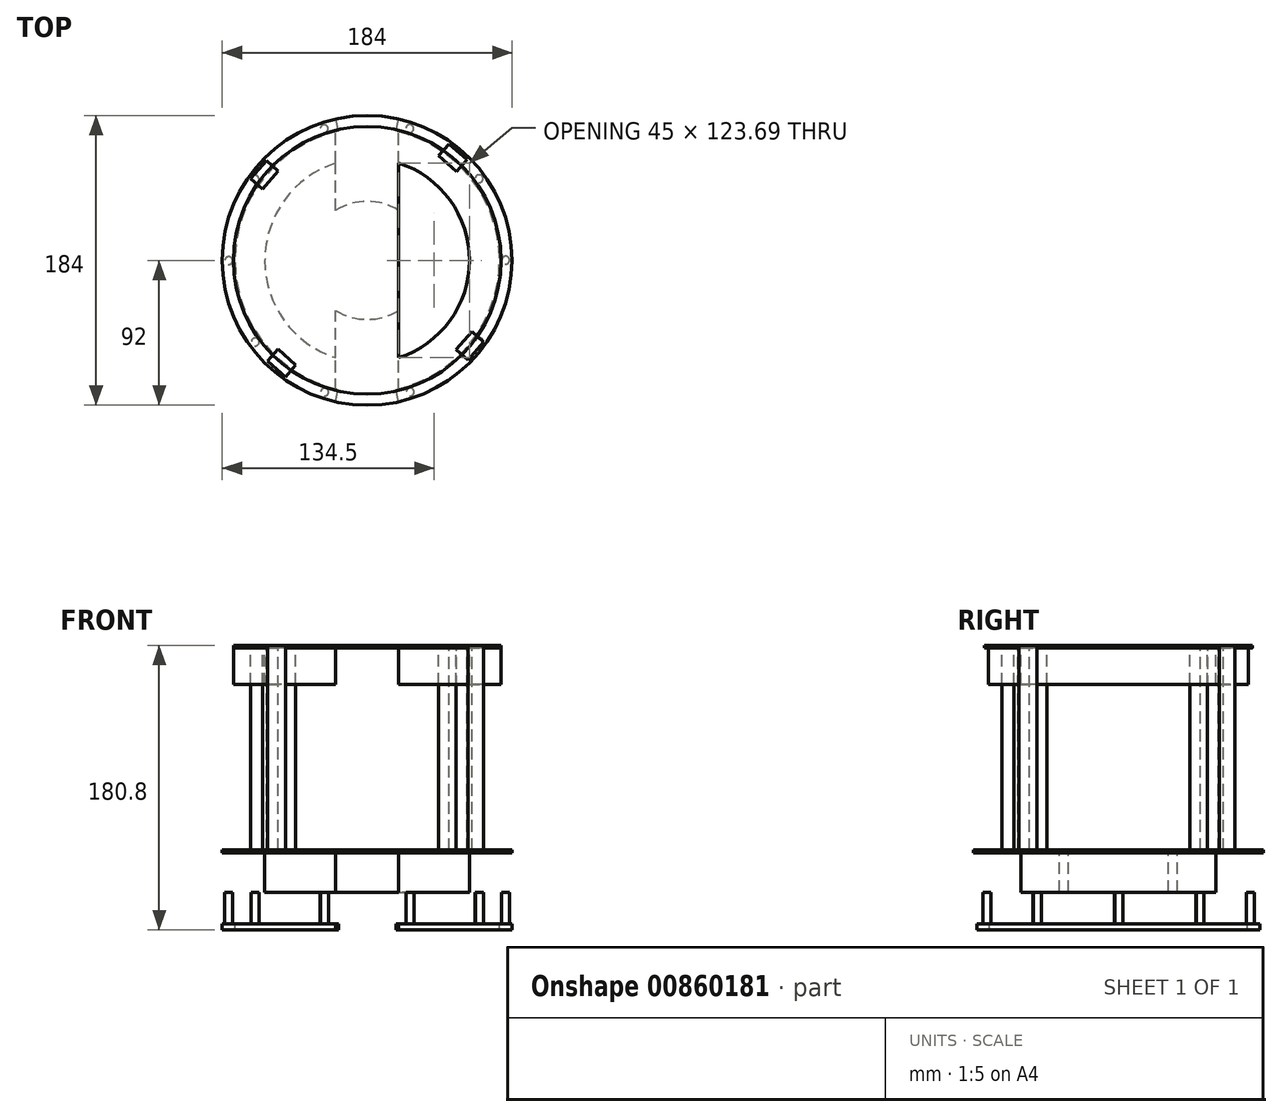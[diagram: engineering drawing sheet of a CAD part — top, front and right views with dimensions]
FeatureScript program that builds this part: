
annotation { "Feature Type Name" : "Feature", "Feature Type Description" : "" }
export const myFeature = defineFeature(function(context is Context, id is Id, definition is map)
    precondition{}
    {
        {
            var Q0;
            Q0=qCreatedBy(makeId("Top.planeOp"),FACE);
            var sketch = newSketch(context, id + "F0", { "sketchPlane" : qUnion([Q0])});
            skCircle(sketch, "E0", {"center": v(0, 0) * mm, "radius": 85 * mm});
            skLineSegment(sketch, "E1", {"start": v(0, 0) * mm, "end": v(15, 0) * mm, "construction": true});
            skLineSegment(sketch, "E2", {"start": v(0, 0) * mm, "end": v(-15, 0) * mm, "construction": true});
            skLineSegment(sketch, "E3", {"start": v(0, 0) * mm, "end": v(0, -65) * mm, "construction": true});
            skLineSegment(sketch, "E4", {"start": v(0, 0) * mm, "end": v(0, 65) * mm, "construction": true});
            skLineSegment(sketch, "E5", {"start": v(0, 65) * mm, "end": v(15, 65) * mm, "construction": true});
            skLineSegment(sketch, "E6", {"start": v(0, 65) * mm, "end": v(-15, 65) * mm, "construction": true});
            skCircle(sketch, "E7", {"center": v(0, 0) * mm, "radius": 65 * mm});
            skLineSegment(sketch, "E8.bottom", {"start": v(20, -93.84) * mm, "end": v(-20, -93.84) * mm});
            skLineSegment(sketch, "E8.top", {"start": v(20, 93.84) * mm, "end": v(-20, 93.84) * mm});
            skLineSegment(sketch, "E8.left", {"start": v(20, -93.84) * mm, "end": v(20, 93.84) * mm});
            skLineSegment(sketch, "E8.right", {"start": v(-20, -93.84) * mm, "end": v(-20, 93.84) * mm});
            skSolve(sketch);
        }
        {
            var Q0;
            Q0=qCreatedBy(makeId("Top.planeOp"),FACE);
            var sketch = newSketch(context, id + "F1", { "sketchPlane" : qUnion([Q0])});
            skCircle(sketch, "E9.0", {"center": v(0, 0) * mm, "radius": 85 * mm});
            skSolve(sketch);
        }
        {
            var Q0;
            Q0=makeQuery(id+"F1.imprint","IMPRINT",FACE,{"disambiguationData":[TD([[makeQuery(id+"F1.imprint","IMPRINT",EDGE,{"derivedFrom":sQuery(id+"F1.wireOp",EDGE,"E9.0")}),1.0]])]});
            extrude(context, id + "F2", {"entities" : qUnion([Q0]), "oppositeDirection" : true, "depth" : 1.8 * mm, "offsetDistance" : 25 * mm});
        }
        {
            var Q0;
            {var subQ0=sQuery(id+"F0.wireOp",EDGE,"E8.left");var subQ1=sQuery(id+"F0.wireOp",EDGE,"E0");var subQ2=makeQuery(id+"F0.imprint","INTERSECT",VERTEX,{"disambiguationData":[OD(0.0)],"derivedFrom":[subQ1,subQ0]});Q0=makeQuery(id+"F0.imprint","IMPRINT",FACE,{"disambiguationData":[TD([[makeQuery(id+"F0.imprint","IMPRINT",EDGE,{"disambiguationData":[TD([[subQ2,1.0]])],"derivedFrom":subQ1}),1.0]])]});}
            var Q1;
            {var subQ0=sQuery(id+"F0.wireOp",EDGE,"E8.right");var subQ1=sQuery(id+"F0.wireOp",EDGE,"E0");var subQ2=makeQuery(id+"F0.imprint","INTERSECT",VERTEX,{"disambiguationData":[OD(0.0)],"derivedFrom":[subQ1,subQ0]});Q1=makeQuery(id+"F0.imprint","IMPRINT",FACE,{"disambiguationData":[TD([[makeQuery(id+"F0.imprint","IMPRINT",EDGE,{"disambiguationData":[TD([[subQ2,-1.0]])],"derivedFrom":subQ1}),1.0]])]});}
            extrude(context, id + "F3", {"entities" : qUnion([Q0, Q1]), "operationType" : NewBodyOperationType.ADD, "oppositeDirection" : true, "depth" : 25 * mm, "offsetDistance" : 25 * mm});
        }
        {
            var Q0;
            {var subQ0=sQuery(id+"F0.wireOp",EDGE,"E8.right");var subQ1=sQuery(id+"F0.wireOp",EDGE,"E0");var subQ2=makeQuery(id+"F0.imprint","INTERSECT",VERTEX,{"disambiguationData":[OD(0.0)],"derivedFrom":[subQ1,subQ0]});Q0=makeQuery(id+"F0.imprint","IMPRINT",FACE,{"disambiguationData":[TD([[makeQuery(id+"F0.imprint","IMPRINT",EDGE,{"disambiguationData":[TD([[subQ2,-1.0]])],"derivedFrom":subQ1}),1.0]])]});}
            var Q1;
            {var subQ0=sQuery(id+"F0.wireOp",EDGE,"E8.right");var subQ1=sQuery(id+"F0.wireOp",EDGE,"E0");var subQ2=makeQuery(id+"F0.imprint","INTERSECT",VERTEX,{"disambiguationData":[OD(0.0)],"derivedFrom":[subQ1,subQ0]});Q1=makeQuery(id+"F0.imprint","IMPRINT",FACE,{"disambiguationData":[TD([[makeQuery(id+"F0.imprint","IMPRINT",EDGE,{"disambiguationData":[TD([[subQ2,1.0]])],"derivedFrom":subQ1}),1.0]])]});}
            var Q2;
            {var subQ0=sQuery(id+"F0.wireOp",EDGE,"E8.left");var subQ1=sQuery(id+"F0.wireOp",EDGE,"E0");var subQ2=makeQuery(id+"F0.imprint","INTERSECT",VERTEX,{"disambiguationData":[OD(0.0)],"derivedFrom":[subQ1,subQ0]});Q2=makeQuery(id+"F0.imprint","IMPRINT",FACE,{"disambiguationData":[TD([[makeQuery(id+"F0.imprint","IMPRINT",EDGE,{"disambiguationData":[TD([[subQ2,1.0]])],"derivedFrom":subQ1}),1.0]])]});}
            var Q3;
            {var subQ0=sQuery(id+"F0.wireOp",EDGE,"E8.right");var subQ1=sQuery(id+"F0.wireOp",EDGE,"E0");var subQ2=makeQuery(id+"F0.imprint","INTERSECT",VERTEX,{"disambiguationData":[OD(1.0)],"derivedFrom":[subQ1,subQ0]});Q3=makeQuery(id+"F0.imprint","IMPRINT",FACE,{"disambiguationData":[TD([[makeQuery(id+"F0.imprint","IMPRINT",EDGE,{"disambiguationData":[TD([[subQ2,-1.0]])],"derivedFrom":subQ1}),1.0]])]});}
            var Q4;
            {var subQ0=sQuery(id+"F0.wireOp",EDGE,"E8.left");var subQ1=sQuery(id+"F0.wireOp",EDGE,"E7");var subQ2=makeQuery(id+"F0.imprint","INTERSECT",VERTEX,{"disambiguationData":[OD(0.0)],"derivedFrom":[subQ1,subQ0]});Q4=makeQuery(id+"F0.imprint","IMPRINT",FACE,{"disambiguationData":[TD([[makeQuery(id+"F0.imprint","IMPRINT",EDGE,{"disambiguationData":[TD([[subQ2,1.0]])],"derivedFrom":subQ1}),1.0]])]});}
            var Q5;
            {var subQ0=sQuery(id+"F0.wireOp",EDGE,"E8.right");var subQ1=sQuery(id+"F0.wireOp",EDGE,"E7");var subQ2=makeQuery(id+"F0.imprint","INTERSECT",VERTEX,{"disambiguationData":[OD(0.0)],"derivedFrom":[subQ1,subQ0]});Q5=makeQuery(id+"F0.imprint","IMPRINT",FACE,{"disambiguationData":[TD([[makeQuery(id+"F0.imprint","IMPRINT",EDGE,{"disambiguationData":[TD([[subQ2,-1.0]])],"derivedFrom":subQ1}),1.0]])]});}
            var Q6;
            {var subQ0=sQuery(id+"F0.wireOp",EDGE,"E8.right");var subQ1=sQuery(id+"F0.wireOp",EDGE,"E7");var subQ2=makeQuery(id+"F0.imprint","INTERSECT",VERTEX,{"disambiguationData":[OD(0.0)],"derivedFrom":[subQ1,subQ0]});Q6=makeQuery(id+"F0.imprint","IMPRINT",FACE,{"disambiguationData":[TD([[makeQuery(id+"F0.imprint","IMPRINT",EDGE,{"disambiguationData":[TD([[subQ2,1.0]])],"derivedFrom":subQ1}),1.0]])]});}
            extrude(context, id + "F4", {"entities" : qUnion([Q0, Q1, Q2, Q3, Q4, Q5, Q6]), "oppositeDirection" : true, "depth" : 1.8 * mm, "offsetDistance" : 25 * mm});
        }
        {
            var Q0;
            {var subQ0=sQuery(id+"F0.wireOp",EDGE,"E0");Q0=makeQuery(id+"F92N3ToIArTKFft_1.boolean.opBoolean","SPLIT",FACE,{"disambiguationData":[TD([makeQuery(id+"FFIeb2ztRoP1rm2_1.boolean.opBoolean","COPY",FACE,{"derivedFrom":makeQuery(id+"FFIeb2ztRoP1rm2_1.opExtrude","SWEPT_FACE",FACE,{"disambiguationData":[OSD([sQuery(id+"FUWerJDIJFKlQu6_1.wireOp",EDGE,"KzpTdK0h-yw9V-XJjy-UJbk-oXAReHN1zFgU.left")])]})})])],"derivedFrom":makeQuery(id+"F4.opExtrude","CAP_FACE",FACE,{"disambiguationData":[OSD([subQ0])],"isStart":true})});}
            var sketch = newSketch(context, id + "F5", { "sketchPlane" : qUnion([Q0])});
            skLineSegment(sketch, "E10", {"start": v(-25, 60) * mm, "end": v(-60.2, 60) * mm, "construction": true});
            skLineSegment(sketch, "E11", {"start": v(-60.2, 60) * mm, "end": v(-45.17, 46.74) * mm, "construction": true});
            skLineSegment(sketch, "E12", {"start": v(-60.2, 60) * mm, "end": v(-56.46, 56.7) * mm});
            skLineSegment(sketch, "E13", {"start": v(-56.46, 56.7) * mm, "end": v(-66.46, 45.34) * mm});
            skLineSegment(sketch, "E14", {"start": v(-66.46, 45.34) * mm, "end": v(-73.96, 51.96) * mm});
            skLineSegment(sketch, "E15", {"start": v(-73.96, 51.96) * mm, "end": v(-63.96, 63.3) * mm});
            skLineSegment(sketch, "E16", {"start": v(-63.96, 63.3) * mm, "end": v(-56.46, 56.7) * mm});
            skSolve(sketch);
        }
        {
            var Q0;
            {var subQ0=sQuery(id+"F5.wireOp",EDGE,"E15");Q0=makeQuery(id+"F5.imprint","IMPRINT",FACE,{"disambiguationData":[TD([[makeQuery(id+"F5.imprint","IMPRINT",EDGE,{"derivedFrom":subQ0}),-1.0]])]});}
            var Q1;
            {var subQ0=sQuery(id+"F5.wireOp",EDGE,"E13");Q1=makeQuery(id+"F5.imprint","IMPRINT",FACE,{"disambiguationData":[TD([[makeQuery(id+"F5.imprint","IMPRINT",EDGE,{"derivedFrom":subQ0}),-1.0]])]});}
            extrude(context, id + "F6", {"entities" : qUnion([Q0, Q1]), "oppositeDirection" : true, "depth" : 130 * mm, "offsetDistance" : 25 * mm});
        }
        {
            var Q0;
            Q0=qCreatedBy(makeId("Right.planeOp"),FACE);
            var sketch = newSketch(context, id + "F7", { "sketchPlane" : qUnion([Q0])});
            skLineSegment(sketch, "E17", {"start": v(0, 0) * mm, "end": v(0, 63.94) * mm, "construction": true});
            skSolve(sketch);
        }
        {
            var Q0;
            Q0=makeQuery(id+"F6.opExtrude","SWEPT_BODY",BODY,{"disambiguationData":[OSD([sQuery(id+"F5.wireOp",EDGE,"E13"),sQuery(id+"F5.wireOp",EDGE,"E14"),sQuery(id+"F5.wireOp",EDGE,"E15"),sQuery(id+"F5.wireOp",EDGE,"E16")])]});
            var Q1;
            Q1=sQuery(id+"F7.wireOp",EDGE,"E17");
            circularPattern(context, id + "F8", {"entities" : qUnion([Q0]), "axis" : qUnion([Q1]), "angle" : 360 * degree, "instanceCount" : 4, "equalSpace" : true});
        }
        {
            var Q0;
            Q0=makeQuery(id+"F6.opExtrude","CAP_FACE",FACE,{"disambiguationData":[OSD([sQuery(id+"F5.wireOp",EDGE,"E13"),sQuery(id+"F5.wireOp",EDGE,"E14"),sQuery(id+"F5.wireOp",EDGE,"E15"),sQuery(id+"F5.wireOp",EDGE,"E16")])],"isStart":false});
            var sketch = newSketch(context, id + "F9", { "sketchPlane" : qUnion([Q0])});
            skCircle(sketch, "E18", {"center": v(0, 0) * mm, "radius": 92 * mm});
            skSolve(sketch);
        }
        {
            var Q0;
            Q0=makeQuery(id+"F9.imprint","IMPRINT",FACE,{"disambiguationData":[TD([[makeQuery(id+"F9.imprint","IMPRINT",EDGE,{"derivedFrom":sQuery(id+"F9.wireOp",EDGE,"E18")}),1.0]])]});
            var Q1;
            Q1=makeQuery(id+"F9.imprint","IMPRINT",FACE,{"disambiguationData":[TD([[makeQuery(id+"F9.imprint","IMPRINT",EDGE,{"derivedFrom":makeQuery(id+"F6.opExtrude","CAP_EDGE",EDGE,{"disambiguationData":[OSD([sQuery(id+"F5.wireOp",EDGE,"E13")])],"isStart":false})}),1.0]])]});
            extrude(context, id + "F10", {"entities" : qUnion([Q0, Q1]), "depth" : 1.8 * mm, "offsetDistance" : 25 * mm});
        }
        {
            var Q0;
            Q0=makeQuery(id+"F10.opExtrude","CAP_FACE",FACE,{"disambiguationData":[OSD([sQuery(id+"F9.wireOp",EDGE,"E18")])],"isStart":false});
            var sketch = newSketch(context, id + "F11", { "sketchPlane" : qUnion([Q0])});
            skCircle(sketch, "E19.0", {"center": v(0, 0) * mm, "radius": 65 * mm});
            skCircle(sketch, "E20.0", {"center": v(0, 0) * mm, "radius": 92 * mm});
            skLineSegment(sketch, "E21.0", {"start": v(20, 93.84) * mm, "end": v(20, -93.84) * mm});
            skLineSegment(sketch, "E21.1", {"start": v(20, 93.84) * mm, "end": v(-20, 93.84) * mm});
            skLineSegment(sketch, "E21.2", {"start": v(-20, 93.84) * mm, "end": v(-20, -93.84) * mm});
            skLineSegment(sketch, "E21.3", {"start": v(20, -93.84) * mm, "end": v(-20, -93.84) * mm});
            skCircle(sketch, "E22", {"center": v(0, 0) * mm, "radius": 37.5 * mm});
            skSolve(sketch);
        }
        {
            var Q0;
            {var subQ0=sQuery(id+"F11.wireOp",EDGE,"E21.0");var subQ1=sQuery(id+"F11.wireOp",EDGE,"E19.0");var subQ2=makeQuery(id+"F11.imprint","INTERSECT",VERTEX,{"disambiguationData":[OD(0.0)],"derivedFrom":[subQ1,subQ0]});Q0=makeQuery(id+"F11.imprint","IMPRINT",FACE,{"disambiguationData":[TD([[makeQuery(id+"F11.imprint","IMPRINT",EDGE,{"disambiguationData":[TD([[subQ2,-1.0]])],"derivedFrom":subQ1}),1.0]])]});}
            var Q1;
            {var subQ0=sQuery(id+"F11.wireOp",EDGE,"E21.2");var subQ1=sQuery(id+"F11.wireOp",EDGE,"E19.0");var subQ2=makeQuery(id+"F11.imprint","INTERSECT",VERTEX,{"disambiguationData":[OD(0.0)],"derivedFrom":[subQ1,subQ0]});Q1=makeQuery(id+"F11.imprint","IMPRINT",FACE,{"disambiguationData":[TD([[makeQuery(id+"F11.imprint","IMPRINT",EDGE,{"disambiguationData":[TD([[subQ2,1.0]])],"derivedFrom":subQ1}),1.0]])]});}
            var Q2;
            {var subQ0=sQuery(id+"F11.wireOp",EDGE,"E22");var subQ1=sQuery(id+"F11.wireOp",EDGE,"E21.0");var subQ2=makeQuery(id+"F11.imprint","INTERSECT",VERTEX,{"disambiguationData":[OD(0.0)],"derivedFrom":[subQ1,subQ0]});Q2=makeQuery(id+"F11.imprint","IMPRINT",FACE,{"disambiguationData":[TD([[makeQuery(id+"F11.imprint","IMPRINT",EDGE,{"disambiguationData":[TD([[subQ2,-1.0]])],"derivedFrom":subQ1}),1.0]])]});}
            var Q3;
            {var subQ0=sQuery(id+"F11.wireOp",EDGE,"E22");var subQ1=sQuery(id+"F11.wireOp",EDGE,"E21.0");var subQ2=makeQuery(id+"F11.imprint","INTERSECT",VERTEX,{"disambiguationData":[OD(0.0)],"derivedFrom":[subQ1,subQ0]});Q3=makeQuery(id+"F11.imprint","IMPRINT",FACE,{"disambiguationData":[TD([[makeQuery(id+"F11.imprint","IMPRINT",EDGE,{"disambiguationData":[TD([[subQ2,-1.0]])],"derivedFrom":subQ1}),-1.0]])]});}
            var Q4;
            {var subQ0=sQuery(id+"F11.wireOp",EDGE,"E22");var subQ1=sQuery(id+"F11.wireOp",EDGE,"E21.2");var subQ2=makeQuery(id+"F11.imprint","INTERSECT",VERTEX,{"disambiguationData":[OD(0.0)],"derivedFrom":[subQ1,subQ0]});Q4=makeQuery(id+"F11.imprint","IMPRINT",FACE,{"disambiguationData":[TD([[makeQuery(id+"F11.imprint","IMPRINT",EDGE,{"disambiguationData":[TD([[subQ2,-1.0]])],"derivedFrom":subQ1}),-1.0]])]});}
            extrude(context, id + "F12", {"entities" : qUnion([Q0, Q1, Q2, Q3, Q4]), "operationType" : NewBodyOperationType.ADD, "depth" : 25 * mm, "offsetDistance" : 25 * mm});
        }
        {
            var Q0;
            Q0=makeQuery(id+"F12.opExtrude","CAP_FACE",FACE,{"disambiguationData":[OSD([sQuery(id+"F11.wireOp",EDGE,"E19.0"),sQuery(id+"F11.wireOp",EDGE,"E20.0"),sQuery(id+"F11.wireOp",EDGE,"E21.0")])],"isStart":false});
            var sketch = newSketch(context, id + "F13", { "sketchPlane" : qUnion([Q0])});
            skCircle(sketch, "E23", {"center": v(27.32, 83.61) * mm, "radius": 2.5 * mm});
            skSolve(sketch);
        }
        {
            var Q0;
            Q0=makeQuery(id+"F13.imprint","IMPRINT",FACE,{"disambiguationData":[TD([[makeQuery(id+"F13.imprint","IMPRINT",EDGE,{"derivedFrom":sQuery(id+"F13.wireOp",EDGE,"E23")}),1.0]])]});
            extrude(context, id + "F14", {"entities" : qUnion([Q0]), "depth" : 20 * mm, "offsetDistance" : 25 * mm});
        }
        {
            var Q0;
            Q0=qCreatedBy(makeId("Right.planeOp"),FACE);
            var sketch = newSketch(context, id + "F15", { "sketchPlane" : qUnion([Q0])});
            skLineSegment(sketch, "E24", {"start": v(0, 0) * mm, "end": v(0, -102.59) * mm, "construction": true});
            skSolve(sketch);
        }
        {
            var Q0;
            Q0=makeQuery(id+"F14.opExtrude","SWEPT_BODY",BODY,{"disambiguationData":[OSD([sQuery(id+"F13.wireOp",EDGE,"E23")])]});
            var Q1;
            Q1=sQuery(id+"F15.wireOp",EDGE,"E24");
            circularPattern(context, id + "F16", {"entities" : qUnion([Q0]), "axis" : qUnion([Q1]), "angle" : 360 * degree, "instanceCount" : 10, "oppositeDirection" : true, "equalSpace" : true});
        }
        {
            var Q0;
            Q0=makeQuery(id+"F16.opPattern","COPY",FACE,{"derivedFrom":makeQuery(id+"F14.opExtrude","CAP_FACE",FACE,{"disambiguationData":[OSD([sQuery(id+"F13.wireOp",EDGE,"E23")])],"isStart":false}),"instanceName":"9"});
            var sketch = newSketch(context, id + "F17", { "sketchPlane" : qUnion([Q0])});
            skArc(sketch, "E25.0", {"start": v(-20, 89.8) * mm, "mid": v(-92, 0) * mm, "end": v(-20, -89.8) * mm});
            skArc(sketch, "E26.0", {"start": v(-18.26, 82) * mm, "mid": v(-84, 0) * mm, "end": v(-18.26, -82) * mm});
            skLineSegment(sketch, "E27", {"start": v(-20, 89.8) * mm, "end": v(-18.26, 82) * mm});
            skArc(sketch, "E28.0", {"start": v(18.26, -82) * mm, "mid": v(84, 0) * mm, "end": v(18.26, 82) * mm});
            skArc(sketch, "E29.0", {"start": v(20, -89.8) * mm, "mid": v(92, 0) * mm, "end": v(20, 89.8) * mm});
            skLineSegment(sketch, "E30", {"start": v(20, 89.8) * mm, "end": v(18.26, 82) * mm});
            skLineSegment(sketch, "E31", {"start": v(-18.26, -82) * mm, "end": v(-20, -89.8) * mm});
            skLineSegment(sketch, "E32", {"start": v(18.26, -82) * mm, "end": v(20, -89.8) * mm});
            skSolve(sketch);
        }
        {
            var Q0;
            Q0=makeQuery(id+"F17.imprint","IMPRINT",FACE,{"disambiguationData":[TD([[makeQuery(id+"F17.imprint","IMPRINT",EDGE,{"derivedFrom":sQuery(id+"F17.wireOp",EDGE,"E28.0")}),-1.0]])]});
            var Q1;
            Q1=makeQuery(id+"F17.imprint","IMPRINT",FACE,{"disambiguationData":[TD([[makeQuery(id+"F17.imprint","IMPRINT",EDGE,{"derivedFrom":makeQuery(id+"F16.opPattern","COPY",EDGE,{"derivedFrom":makeQuery(id+"F14.opExtrude","CAP_EDGE",EDGE,{"disambiguationData":[OSD([sQuery(id+"F13.wireOp",EDGE,"E23")])],"isStart":false}),"instanceName":"9"})}),1.0]])]});
            var Q2;
            Q2=makeQuery(id+"F17.imprint","IMPRINT",FACE,{"disambiguationData":[TD([[makeQuery(id+"F17.imprint","IMPRINT",EDGE,{"derivedFrom":sQuery(id+"F17.wireOp",EDGE,"E25.0")}),1.0]])]});
            extrude(context, id + "F18", {"entities" : qUnion([Q0, Q1, Q2]), "depth" : 4 * mm, "offsetDistance" : 25 * mm});
        }
    });
